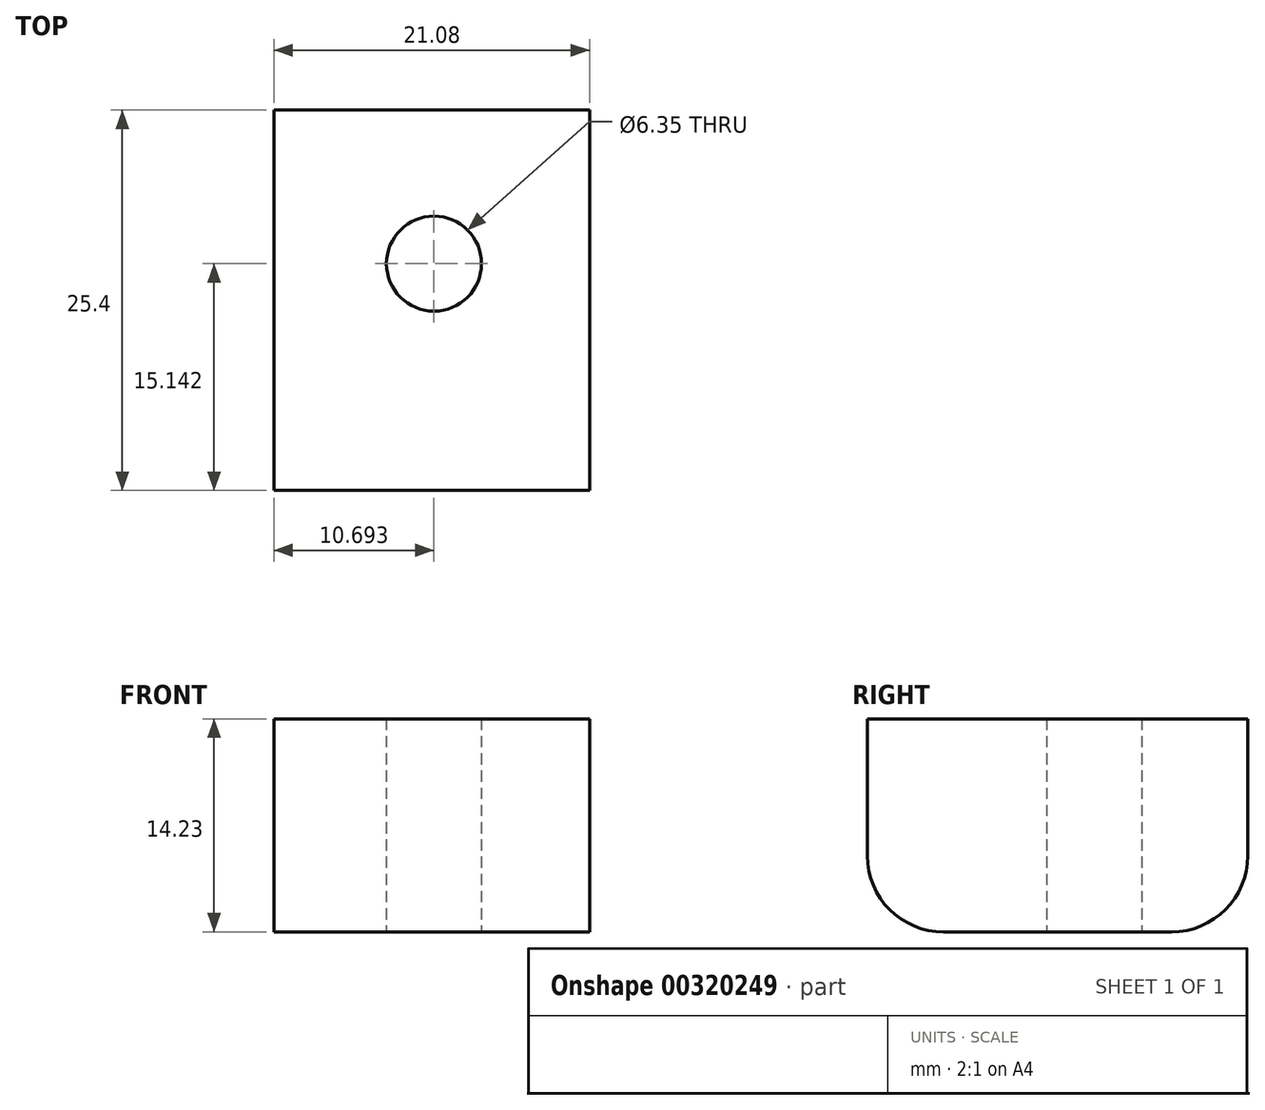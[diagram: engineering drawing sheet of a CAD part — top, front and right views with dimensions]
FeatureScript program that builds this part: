
annotation { "Feature Type Name" : "Feature", "Feature Type Description" : "" }
export const myFeature = defineFeature(function(context is Context, id is Id, definition is map)
    precondition{}
    {
        {
            var Q0;
            Q0=qCreatedBy(makeId("Front.planeOp"),FACE);
            var sketch = newSketch(context, id + "F0", { "sketchPlane" : qUnion([Q0])});
            skLineSegment(sketch, "E0.bottom", {"start": v(0, 0) * mm, "end": v(21.08, 0) * mm});
            skLineSegment(sketch, "E0.top", {"start": v(0, 14.23) * mm, "end": v(21.08, 14.23) * mm});
            skLineSegment(sketch, "E0.left", {"start": v(0, 0) * mm, "end": v(0, 14.23) * mm});
            skLineSegment(sketch, "E0.right", {"start": v(21.08, 0) * mm, "end": v(21.08, 14.23) * mm});
            skSolve(sketch);
        }
        {
            var Q0;
            Q0 = qSketchRegion(id + "F0", true);
            extrude(context, id + "F1", {"entities" : qUnion([Q0]), "depth" : 25.4 * mm});
        }
        {
            var Q0;
            Q0=makeQuery(id+"F1.opExtrude","CAP_EDGE",EDGE,{"disambiguationData":[OSD([sQuery(id+"F0.wireOp",EDGE,"E0.bottom")])],"isStart":false});
            fillet(context, id + "F2", {"entities" : qUnion([Q0]), "radius" : 5.08 * mm, "tangentPropagation" : true, "allowEdgeOverflow" : false});
        }
        {
            var Q0;
            Q0=makeQuery(id+"F1.opExtrude","SWEPT_FACE",FACE,{"disambiguationData":[OSD([sQuery(id+"F0.wireOp",EDGE,"E0.bottom")])]});
            var sketch = newSketch(context, id + "F3", { "sketchPlane" : qUnion([Q0])});
            skCircle(sketch, "E1", {"center": v(10.7, 10.26) * mm, "radius": 3.9 * mm});
            skSolve(sketch);
        }
        {
            var Q0;
            Q0=sQuery(id+"F3.wireOp",VERTEX,"E1.center");
            var Q1;
            Q1=makeQuery(id+"F1.opExtrude","SWEPT_BODY",BODY,{"disambiguationData":[OSD([sQuery(id+"F0.wireOp",EDGE,"E0.bottom"),sQuery(id+"F0.wireOp",EDGE,"E0.top"),sQuery(id+"F0.wireOp",EDGE,"E0.left"),sQuery(id+"F0.wireOp",EDGE,"E0.right")])]});
            hole(context, id + "F4", {"style" : HoleStyle.SIMPLE, "endStyle" : HoleEndStyle.THROUGH, "holeDiameter" : 6.35 * mm, "tappedDepth" : 12.7 * mm, "tapClearance" : 3, "locations" : qUnion([Q0]), "scope" : qUnion([Q1])});
        }
        {
            var Q0;
            Q0=makeQuery(id+"F1.opExtrude","CAP_EDGE",EDGE,{"disambiguationData":[OSD([sQuery(id+"F0.wireOp",EDGE,"E0.bottom")])],"isStart":true});
            fillet(context, id + "F5", {"entities" : qUnion([Q0]), "radius" : 5.08 * mm, "tangentPropagation" : true, "allowEdgeOverflow" : false});
        }
    });
